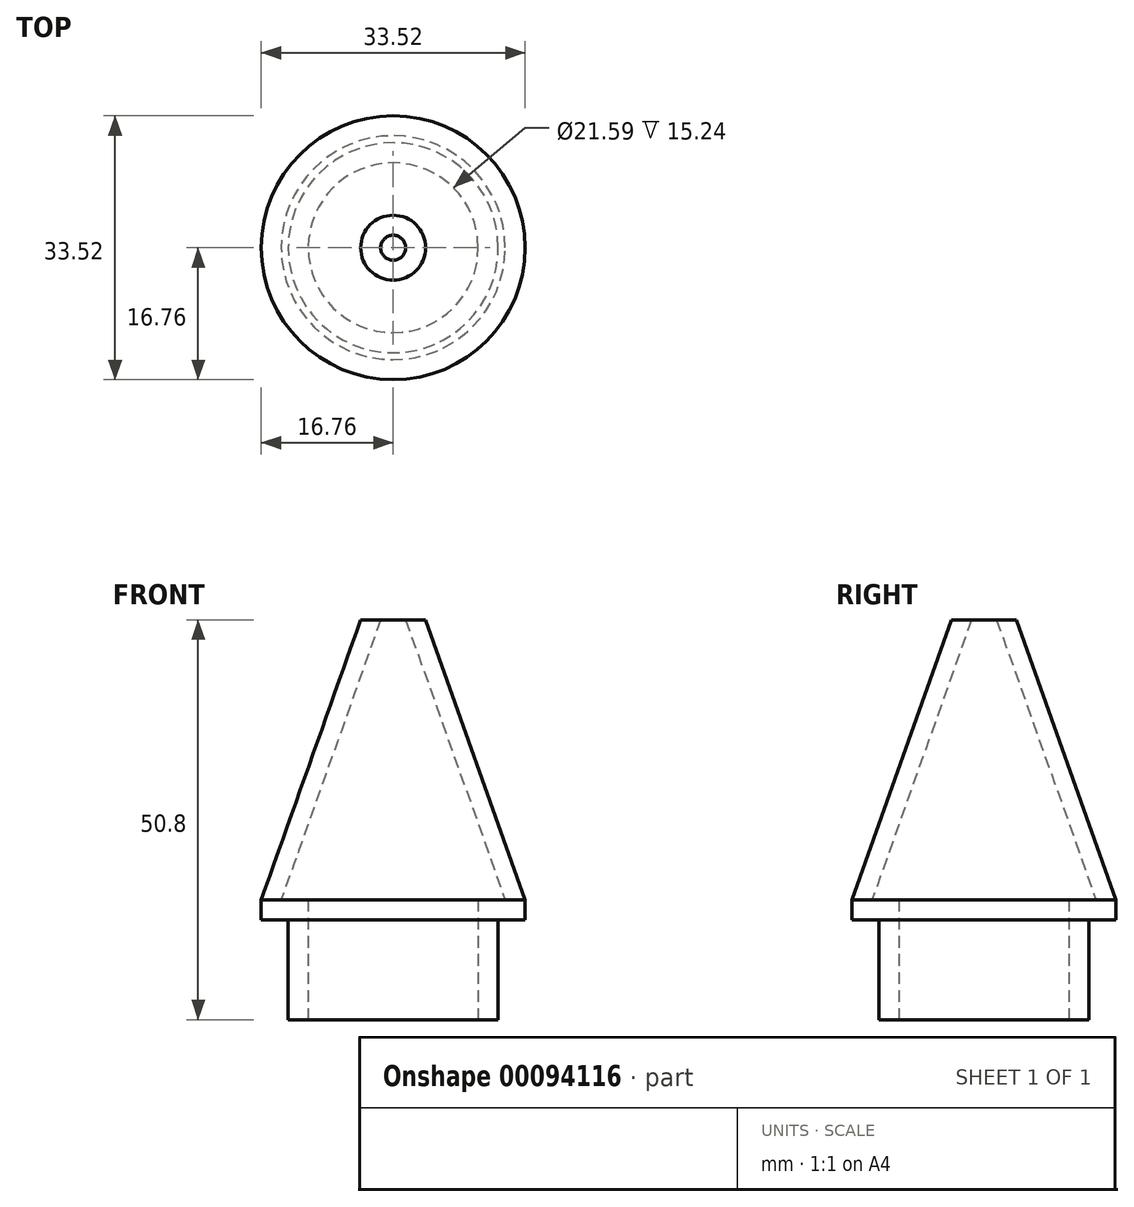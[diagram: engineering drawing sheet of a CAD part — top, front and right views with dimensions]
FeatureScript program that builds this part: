
annotation { "Feature Type Name" : "Feature", "Feature Type Description" : "" }
export const myFeature = defineFeature(function(context is Context, id is Id, definition is map)
    precondition{}
    {
        {
            var Q0;
            Q0=qCreatedBy(makeId("Front.planeOp"),FACE);
            var sketch = newSketch(context, id + "F0", { "sketchPlane" : qUnion([Q0])});
            skLineSegment(sketch, "E0", {"start": v(0, 0) * mm, "end": v(0, 25.78) * mm, "construction": true});
            skLineSegment(sketch, "E1.bottom", {"start": v(10.8, 0) * mm, "end": v(13.34, 0) * mm});
            skLineSegment(sketch, "E1.top", {"start": v(10.8, 12.7) * mm, "end": v(13.34, 12.7) * mm});
            skLineSegment(sketch, "E1.left", {"start": v(10.8, 0) * mm, "end": v(10.8, 12.7) * mm});
            skLineSegment(sketch, "E1.right", {"start": v(13.34, 0) * mm, "end": v(13.34, 12.7) * mm});
            skLineSegment(sketch, "E2.bottom", {"start": v(10.8, 12.7) * mm, "end": v(16.76, 12.7) * mm});
            skLineSegment(sketch, "E2.top", {"start": v(10.8, 15.24) * mm, "end": v(16.76, 15.24) * mm});
            skLineSegment(sketch, "E2.left", {"start": v(10.8, 12.7) * mm, "end": v(10.8, 15.24) * mm});
            skLineSegment(sketch, "E2.right", {"start": v(16.76, 12.7) * mm, "end": v(16.76, 15.24) * mm});
            skLineSegment(sketch, "E3", {"start": v(16.76, 15.24) * mm, "end": v(4.13, 50.8) * mm});
            skLineSegment(sketch, "E4", {"start": v(4.13, 50.8) * mm, "end": v(1.59, 50.8) * mm});
            skLineSegment(sketch, "E5", {"start": v(1.59, 50.8) * mm, "end": v(14.22, 15.24) * mm});
            skSolve(sketch);
        }
        {
            var Q0;
            {var subQ0=sQuery(id+"F0.wireOp",EDGE,"E3");Q0=makeQuery(id+"F0.imprint","IMPRINT",FACE,{"disambiguationData":[TD([[makeQuery(id+"F0.imprint","IMPRINT",EDGE,{"derivedFrom":subQ0}),1.0]])]});}
            var Q1;
            {var subQ3=sQuery(id+"F0.wireOp",EDGE,"E2.left");Q1=makeQuery(id+"F0.imprint","IMPRINT",FACE,{"disambiguationData":[TD([[makeQuery(id+"F0.imprint","IMPRINT",EDGE,{"derivedFrom":subQ3}),-1.0]])]});}
            var Q2;
            Q2=makeQuery(id+"F0.imprint","IMPRINT",FACE,{"disambiguationData":[TD([[makeQuery(id+"F0.imprint","IMPRINT",EDGE,{"derivedFrom":sQuery(id+"F0.wireOp",EDGE,"E1.bottom")}),1.0]])]});
            var Q3;
            Q3=sQuery(id+"F0.wireOp",EDGE,"E0");
            revolve(context, id + "F1", {"entities" : qUnion([Q0, Q1, Q2]), "axis" : qUnion([Q3]), "revolveType" : RevolveType.FULL});
        }
    });
